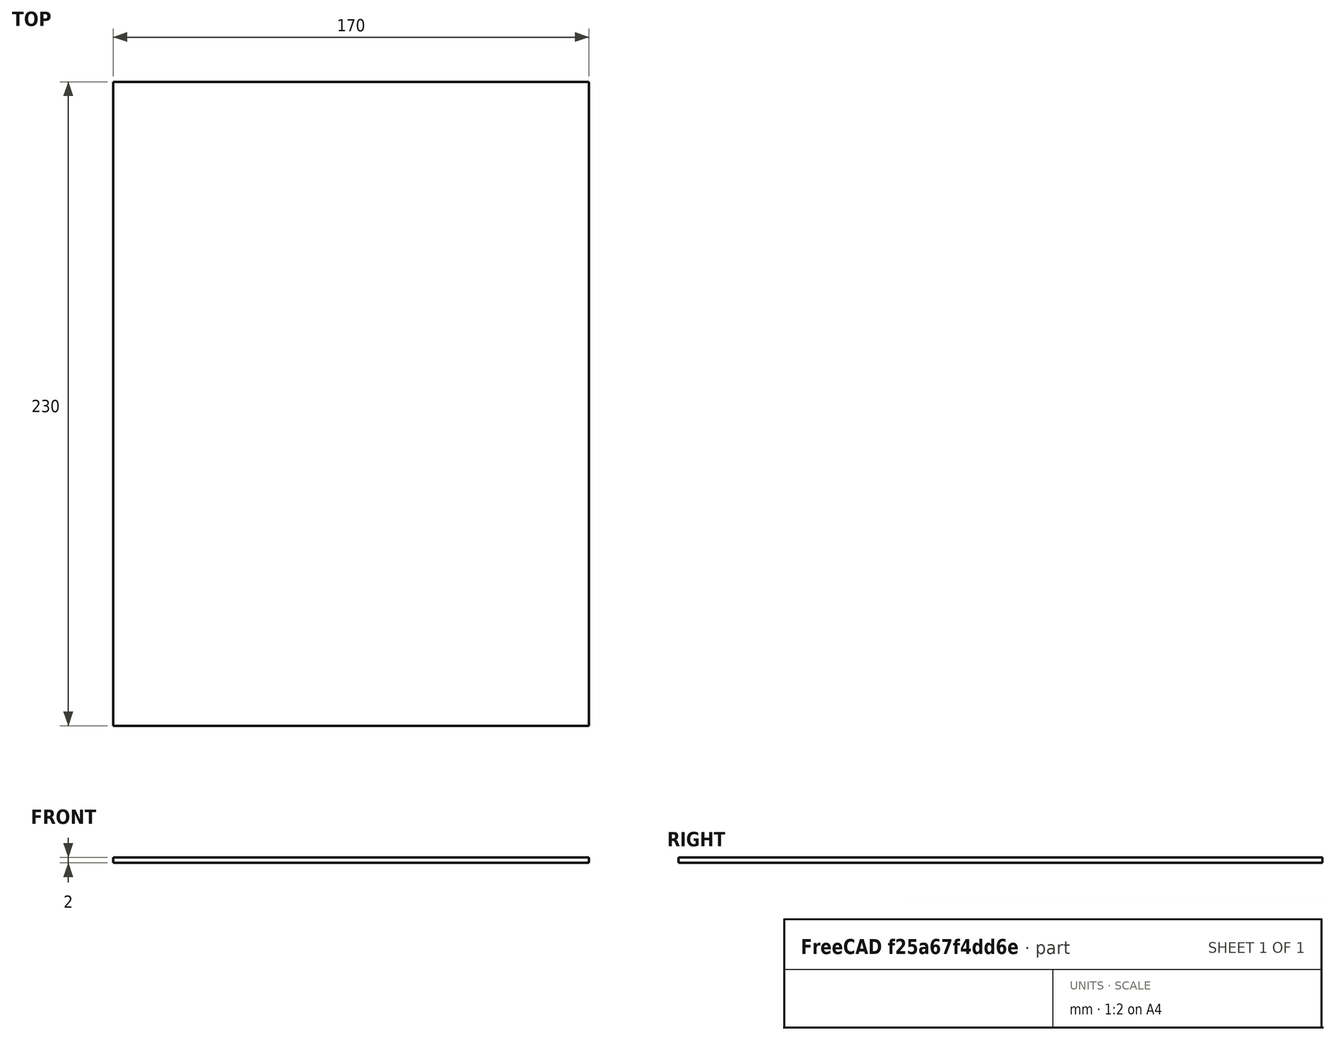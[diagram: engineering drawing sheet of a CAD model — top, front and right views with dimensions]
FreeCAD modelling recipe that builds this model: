
FCSTD DOCUMENT  (FreeCAD 0.17RUnknown)
Label: cam_landing
License: All rights reserved
LicenseURL: http://en.wikipedia.org/wiki/All_rights_reserved
objects: Path::FeaturePython×7, Part::FeaturePython×3, App::FeaturePython×1, Path::FeatureCompoundPython×1
note: 5 computed .brp shape members not serialized (recipe doc carries the construction recipe); baked Part::Feature solids carry a one-line shape summary decoded from their .brp

FEATURE [Path::FeaturePython] Default_Tool  label="Default Tool"  # Path/CAM operation (typed FeaturePython)
  HorizFeed = 10
  HorizRapid = 0
  SpindleDir = 0
  SpindleSpeed = 24000
  ToolNumber = 1
  VertFeed = 1.66667
  VertRapid = 0
  expr: Tool.Diameter = 3.1749999999999998
  expr: VertFeed = 100mm / min
  expr: HorizFeed = 600mm / min
  expr: HorizRapid = SetupSheet.HorizRapid
  expr: VertRapid = SetupSheet.VertRapid
FEATURE [Path::FeaturePython] Contour  # Path/CAM operation (typed FeaturePython)
  Active = true
  AreaParams:
    OpenMode = 0
    Angle = 45.0
    MinArcPoints = 4
    Coplanar = 2
    Tolerance = 1e-07
    CleanDistance = 0.0
    PocketExtraOffset = 0.0
    RoundPrecision = 0.0
    AngleShift = 0.0
    SubjectFill = 0
    PocketMode = 0
    Simplify = False
    SectionTolerance = 1e-06
    MaxArcPoints = 100
    Offset = 1.5875
    Accuracy = 0.01
    PocketStepover = 0.0
    ClipFill = 0
    ToolRadius = 1.0
    Outline = False
    ClipperScale = 10000000.0
    FromCenter = False
    Explode = False
    EndType = 0
    Shift = 0.0
    ExtraPass = 0
    Project = False
    JoinType = 0
    Thicken = False
    Stepdown = 1.0
    SectionMode = 2
    MiterLimit = 2.0
    Deflection = 0.01
    Reorient = True
    FitArcs = True
    SectionCount = -1
    SectionOffset = 0.0
    Stepover = 0.0
    Unit = 1.0
    Fill = 0
  ClearanceHeight = 2
  Direction = 0
  FinalDepth = -3
  JoinType = 0
  MiterLimit = 0.1
  OffsetExtra = 0
  OpFinalDepth = -2
  OpStartDepth = 0
  OpToolDiameter = 3.175
  PathParams = {'resume_height': 3.0, 'feedrate': 10.0, 'verbose': True, 'orientation': 1, 'return_end': True, 'preamble': False, 'retraction': 2.0, 'feedrate_v': 1.666666666667}
  SafeHeight = 3
  Side = 0
  StartDepth = 0
  StartPoint = (0,0,0)
  StepDown = 1
  ToolController = -> Default_Tool
  UseComp = true
  UseStartPoint = false
  expr: ClearanceHeight = StartDepth + SetupSheet.ClearanceHeightOffset
  expr: SafeHeight = StartDepth + SetupSheet.SafeHeightOffset
  expr: StepDown = 1
  expr: FinalDepth = -3
  expr: StartDepth = OpStartDepth
FEATURE [Part::FeaturePython] Stock001  # WARN: FeaturePython — macro-defined, semantics opaque (R4)
  Height = 2
  Length = 170
  Placement = pos=(0,0,-2) rot=(0,0,1;0rad)
  StockType = CreateBox
  Width = 230
FEATURE [App::FeaturePython] SetupSheet  # Path/CAM operation (typed FeaturePython)
  ClearanceHeightExpression = StartDepth+SetupSheet.ClearanceHeightOffset
  ClearanceHeightOffset = 2
  FinalDepthExpression = OpFinalDepth
  HorizRapid = 0
  SafeHeightExpression = StartDepth+SetupSheet.SafeHeightOffset
  SafeHeightOffset = 3
  StartDepthExpression = OpStartDepth
  StepDownExpression = OpToolDiameter
  VertRapid = 0
FEATURE [Path::FeaturePython] T2__drill  label="T2: drill"  # Path/CAM operation (typed FeaturePython)
  HorizFeed = 10
  HorizRapid = 0
  SpindleDir = 0
  SpindleSpeed = 12000
  ToolNumber = 2
  VertFeed = 1.66667
  VertRapid = 0
  expr: VertFeed = 100mm / min
  expr: HorizFeed = 600mm / min
  expr: HorizRapid = SetupSheet.HorizRapid
  expr: VertRapid = SetupSheet.VertRapid
FEATURE [Path::FeaturePython] TagDressup  # Path/CAM operation (typed FeaturePython)
  Angle = 75
  Base = -> Contour
  Height = 2.5
  Positions = (5) [(54.2136,41.5875,0),(0.314424,21,0),(104.586,21.0466,0),(73.5363,0.4125,0),(34.8909,0.4125,0)]
  Radius = 1
  SegmentationFactor = 50
  Width = 2.79
FEATURE [Part::FeaturePython] landing_01  # a2plus imported part (geometry in sourceFile) (typed FeaturePython)
  Placement = pos=(19.9645,61.58,-2) rot=(0,0,1;0rad)
  fixedPosition = false
  sourceFile = <userpath>/hs/fly/cad/landing.fcstd
  timeLastImport = 1.5368e+09
  updateColors = true
FEATURE [Part::FeaturePython] Clone  label="Base-arm_01"  # Draft clone (typed FeaturePython)
  AttacherType = Attacher::AttachEngine3D
  Fuse = false
  Objects = -> [landing_01]
  PathResource = Base
  Placement = pos=(42,21,-2) rot=(0,0,1;1.5708rad)
  Scale = (1,1,1)
FEATURE [Path::FeaturePython] Pocket_Shape001  # Path/CAM operation (typed FeaturePython)
  Active = true
  AreaParams:
    OpenMode = 0
    Angle = 45.0
    MinArcPoints = 4
    Coplanar = 0
    Tolerance = 1e-07
    CleanDistance = 0.0
    PocketExtraOffset = 0.0
    RoundPrecision = 0.0
    AngleShift = 0.0
    SubjectFill = 0
    PocketMode = 2
    Simplify = False
    SectionTolerance = 1e-06
    MaxArcPoints = 100
    Offset = 0.0
    Accuracy = 0.01
    PocketStepover = 3.175
    ClipFill = 0
    ToolRadius = 1.5875
    Outline = False
    ClipperScale = 10000000.0
    FromCenter = True
    Explode = False
    EndType = 0
    Shift = 0.0
    ExtraPass = 0
    Project = False
    JoinType = 0
    Thicken = False
    Stepdown = 1.0
    SectionMode = 2
    MiterLimit = 2.0
    Deflection = 0.01
    Reorient = True
    FitArcs = True
    SectionCount = -1
    SectionOffset = 0.0
    Stepover = 0.0
    Unit = 1.0
    Fill = 0
  Base = -> [Clone]
  ClearanceHeight = 2
  CutMode = 0
  ExtraOffset = 0
  FinalDepth = -2
  FinishDepth = 0
  KeepToolDown = false
  MinTravel = false
  OffsetPattern = 1
  OpFinalDepth = -2
  OpStartDepth = 0
  OpToolDiameter = 3.175
  PathParams = {'resume_height': 3.0, 'feedrate': 10.0, 'verbose': True, 'orientation': 1, 'return_end': True, 'preamble': False, 'retraction': 2.0, 'feedrate_v': 1.666666666667}
  SafeHeight = 3
  StartAt = 0
  StartDepth = 0
  StartPoint = (0,0,0)
  StepDown = 0.5
  StepOver = 100
  ToolController = -> Default_Tool
  UseStartPoint = false
  ZigZagAngle = 45
  expr: ClearanceHeight = StartDepth + SetupSheet.ClearanceHeightOffset
  expr: SafeHeight = StartDepth + SetupSheet.SafeHeightOffset
  expr: StepDown = 0.5
  expr: FinalDepth = OpFinalDepth
  expr: StartDepth = OpStartDepth
FEATURE [Path::FeaturePython] Drilling  # Path/CAM operation (typed FeaturePython)
  Active = true
  AddTipLength = false
  Base = -> [Clone]
  ClearanceHeight = 2
  DwellEnabled = false
  DwellTime = 0
  FinalDepth = -4
  OpFinalDepth = -2
  OpStartDepth = 0
  OpToolDiameter = 3
  PeckDepth = 0
  PeckEnabled = false
  RetractHeight = 10
  ReturnLevel = 0
  SafeHeight = 3
  StartDepth = 0
  ToolController = -> T2__drill
  expr: ClearanceHeight = StartDepth + SetupSheet.ClearanceHeightOffset
  expr: SafeHeight = StartDepth + SetupSheet.SafeHeightOffset
  expr: FinalDepth = -4
  expr: StartDepth = OpStartDepth
FEATURE [Path::FeatureCompoundPython] Operations  # Path/CAM operation (typed FeaturePython)
  Group = -> [Drilling,Pocket_Shape001,TagDressup]
  UsePlacements = false
FEATURE [Path::FeaturePython] Job  # Path/CAM operation (typed FeaturePython)
  Base = -> Clone
  GeometryTolerance = 0.01
  Operations = -> Operations
  PostProcessor = 5
  PostProcessorOutputFile = <userpath>/hs/fly/cad/gcode/arm
  SetupSheet = -> SetupSheet
  Stock = -> Stock001
  ToolController = -> [Default_Tool,T2__drill]
